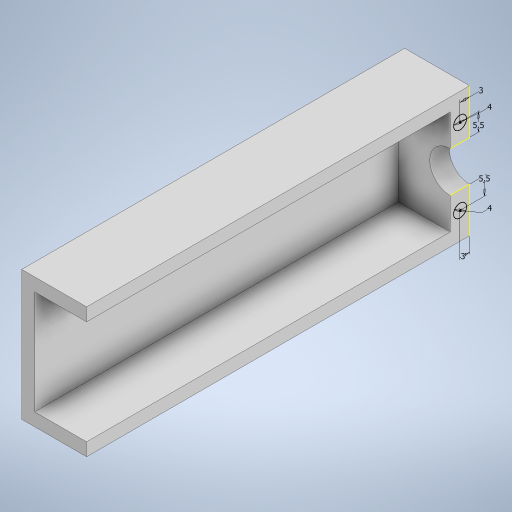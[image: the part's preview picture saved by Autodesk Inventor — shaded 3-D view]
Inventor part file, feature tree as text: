
AUTODESK INVENTOR PART (.ipt)
format: ipt  version: 2023 (Build 270158000, 158)  size: 259,584 bytes
history: native  units: in
note: dims shown in document units (in); Inventor stores cm internally (conversion verified against a paired STEP export)
features: sketch x3, extrude x2, other x1
ambient origin geometry x8: Origin, YZ Plane, XZ Plane, XY Plane, X Axis, Y Axis, Z Axis, Center Point
bodies: Body1 (feature_tree)
feature tree (6):
  other  "솔리드1"
  extrude  "돌출1"  Depth=0.7874in
  extrude  "돌출2"  Depth=1.5748in
  sketch  "스케치4"
  sketch  "스케치1"
  sketch  "스케치2"
